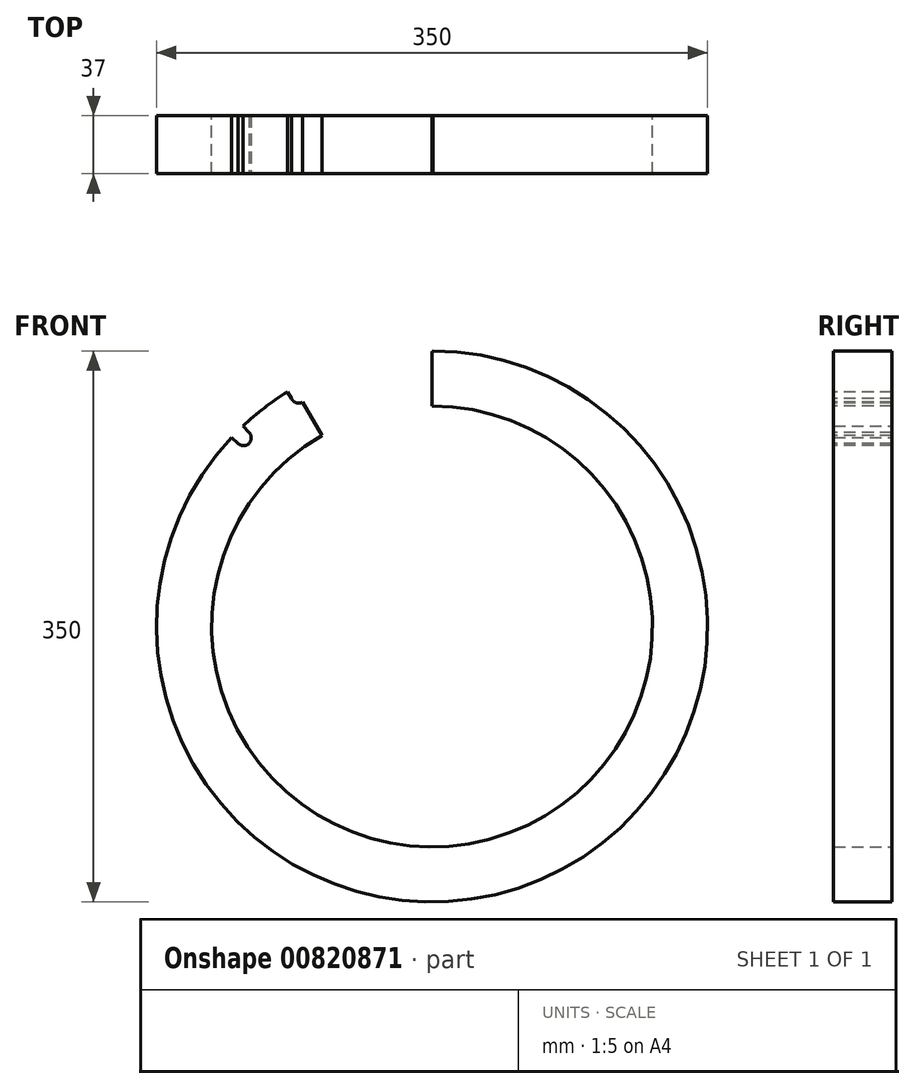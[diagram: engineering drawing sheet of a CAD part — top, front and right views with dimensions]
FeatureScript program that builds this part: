
annotation { "Feature Type Name" : "Feature", "Feature Type Description" : "" }
export const myFeature = defineFeature(function(context is Context, id is Id, definition is map)
    precondition{}
    {
        {
            var Q0;
            Q0=qCreatedBy(makeId("Front.planeOp"),FACE);
            var sketch = newSketch(context, id + "F0", { "sketchPlane" : qUnion([Q0])});
            skCircle(sketch, "E0", {"center": v(0, 0) * mm, "radius": 175 * mm});
            skCircle(sketch, "E1", {"center": v(0, 0) * mm, "radius": 140 * mm});
            skSolve(sketch);
        }
        {
            var Q0;
            Q0 = qSketchRegion(id + "F0", true);
            extrude(context, id + "F1", {"entities" : qUnion([Q0]), "depth" : 37 * mm, "offsetDistance" : 25 * mm});
        }
        {
            var Q0;
            Q0=makeQuery(id+"F1.opExtrude","CAP_FACE",FACE,{"disambiguationData":[OSD([sQuery(id+"F0.wireOp",EDGE,"E0"),sQuery(id+"F0.wireOp",EDGE,"E1")])],"isStart":false});
            var sketch = newSketch(context, id + "F2", { "sketchPlane" : qUnion([Q0])});
            skLineSegment(sketch, "E2", {"start": v(0, 0) * mm, "end": v(0, 175) * mm});
            skLineSegment(sketch, "E3.MirrorCS", {"start": v(-127.59, 134.66) * mm, "end": v(-116.27, 123.34) * mm});
            skLineSegment(sketch, "E4.MirrorCS", {"start": v(-134.66, 127.59) * mm, "end": v(-123.34, 116.27) * mm});
            skArc(sketch, "E5.MirrorCS", {"start": v(-134.66, 127.59) * mm, "mid": v(-134.7, 134.7) * mm, "end": v(-127.59, 134.66) * mm});
            skPoint(sketch, "E6", {"position": v(0, 175) * mm});
            skCircle(sketch, "E7", {"center": v(0, 175) * mm, "radius": 0.5 * mm});
            skPoint(sketch, "E8.center.orphan", {"position": v(0, 169) * mm});
            skArc(sketch, "E9", {"start": v(-123.34, 116.27) * mm, "mid": v(-116.32, 116.32) * mm, "end": v(-116.27, 123.34) * mm});
            skLineSegment(sketch, "E10.MirrorCS", {"start": v(-97.03, 158.1) * mm, "end": v(-89.4, 144.87) * mm});
            skArc(sketch, "E11.MirrorCS", {"start": v(-80.65, 149.65) * mm, "mid": v(-82.25, 142.46) * mm, "end": v(-89.28, 144.67) * mm});
            skLineSegment(sketch, "E12.MirrorCS", {"start": v(-88.4, 163.08) * mm, "end": v(-80.65, 149.65) * mm});
            skArc(sketch, "E13.MirrorCS", {"start": v(-88.39, 163.09) * mm, "mid": v(-95.25, 164.98) * mm, "end": v(-97.05, 158.09) * mm});
            skLineSegment(sketch, "E14", {"start": v(-89.28, 144.67) * mm, "end": v(-89.4, 144.87) * mm});
            skLineSegment(sketch, "E15", {"start": v(-84.75, 146.8) * mm, "end": v(0, 0) * mm});
            skLineSegment(sketch, "E16", {"start": v(-119.85, 119.85) * mm, "end": v(0, 0) * mm});
            skSolve(sketch);
        }
        {
            var Q0;
            {var subQ0=sQuery(id+"F2.wireOp",EDGE,"E3.MirrorCS");Q0=makeQuery(id+"F2.imprint","IMPRINT",FACE,{"disambiguationData":[TD([[makeQuery(id+"F2.imprint","IMPRINT",EDGE,{"derivedFrom":subQ0}),-1.0]])]});}
            var Q1;
            {var subQ1=sQuery(id+"F2.wireOp",EDGE,"E10.MirrorCS");Q1=makeQuery(id+"F2.imprint","IMPRINT",FACE,{"disambiguationData":[TD([[makeQuery(id+"F2.imprint","IMPRINT",EDGE,{"derivedFrom":subQ1}),1.0]])]});}
            var Q2;
            {var subQ1=sQuery(id+"F2.wireOp",EDGE,"E11.MirrorCS");Q2=makeQuery(id+"F2.imprint","IMPRINT",FACE,{"disambiguationData":[TD([[makeQuery(id+"F2.imprint","IMPRINT",EDGE,{"derivedFrom":subQ1}),-1.0]])]});}
            extrude(context, id + "F3", {"entities" : qUnion([Q0, Q1, Q2]), "operationType" : NewBodyOperationType.REMOVE, "oppositeDirection" : true, "depth" : 64 * mm, "offsetDistance" : 25 * mm});
        }
        {
            var Q0;
            Q0 = qSketchRegion(id + "F2", true);
            extrude(context, id + "F4", {"entities" : qUnion([Q0]), "operationType" : NewBodyOperationType.REMOVE, "oppositeDirection" : true, "depth" : 40 * mm, "offsetDistance" : 25 * mm});
        }
    });
